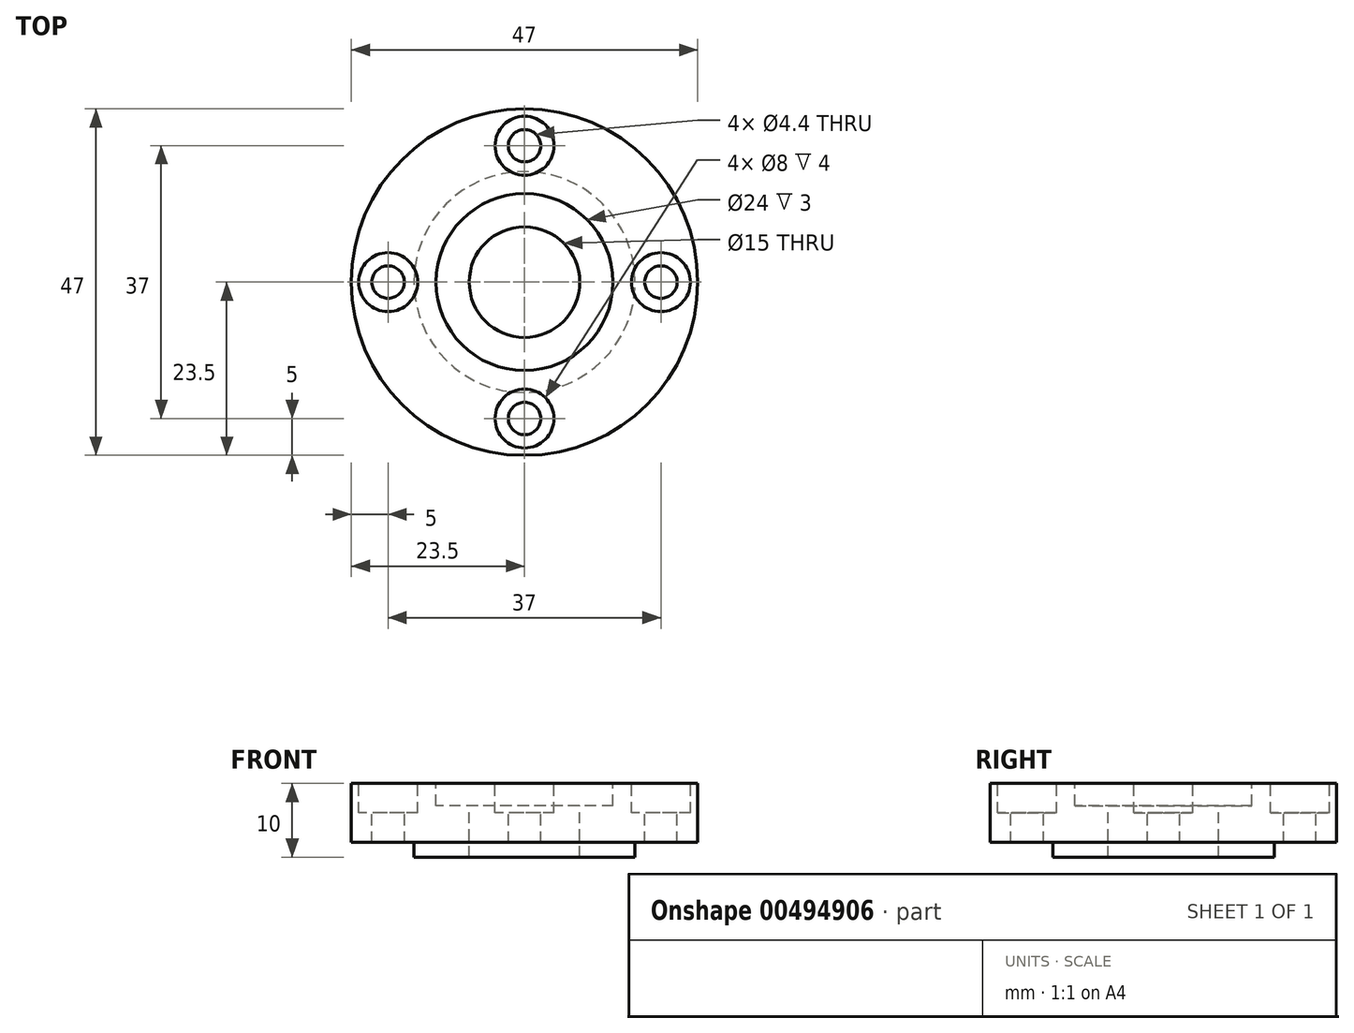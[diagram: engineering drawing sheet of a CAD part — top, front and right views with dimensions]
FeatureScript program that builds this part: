
annotation { "Feature Type Name" : "Feature", "Feature Type Description" : "" }
export const myFeature = defineFeature(function(context is Context, id is Id, definition is map)
    precondition{}
    {
        {
            var Q0;
            Q0=qCreatedBy(makeId("Top.planeOp"),FACE);
            var sketch = newSketch(context, id + "F0", { "sketchPlane" : qUnion([Q0])});
            skCircle(sketch, "E0", {"center": v(0, 0) * mm, "radius": 15 * mm});
            skSolve(sketch);
        }
        {
            var Q0;
            Q0=qSketchRegion(id+"F0",true);
            extrude(context, id + "F1", {"entities" : qUnion([Q0]), "oppositeDirection" : true, "depth" : 2 * mm});
        }
        {
            var Q0;
            Q0=qCreatedBy(makeId("Top.planeOp"),FACE);
            var sketch = newSketch(context, id + "F2", { "sketchPlane" : qUnion([Q0])});
            skCircle(sketch, "E1", {"center": v(0, 0) * mm, "radius": 23.5 * mm});
            skSolve(sketch);
        }
        {
            var Q0;
            Q0=qSketchRegion(id+"F2",true);
            extrude(context, id + "F3", {"entities" : qUnion([Q0]), "operationType" : NewBodyOperationType.ADD, "depth" : 8 * mm});
        }
        {
            var Q0;
            Q0=makeQuery(id+"F3.opExtrude","CAP_FACE",FACE,{"disambiguationData":[OSD([sQuery(id+"F2.wireOp",EDGE,"E1")])],"isStart":false});
            var sketch = newSketch(context, id + "F4", { "sketchPlane" : qUnion([Q0])});
            skCircle(sketch, "E2", {"center": v(0, 0) * mm, "radius": 12 * mm});
            skSolve(sketch);
        }
        {
            var Q0;
            Q0=qSketchRegion(id+"F4",true);
            extrude(context, id + "F5", {"entities" : qUnion([Q0]), "operationType" : NewBodyOperationType.REMOVE, "oppositeDirection" : true, "depth" : 3 * mm});
        }
        {
            var Q0;
            Q0=makeQuery(id+"F5.boolean.opBoolean","COPY",FACE,{"derivedFrom":makeQuery(id+"F5.opExtrude","CAP_FACE",FACE,{"disambiguationData":[OSD([sQuery(id+"F4.wireOp",EDGE,"E2")])],"isStart":false})});
            var sketch = newSketch(context, id + "F6", { "sketchPlane" : qUnion([Q0])});
            skCircle(sketch, "E3", {"center": v(0, 0) * mm, "radius": 7.5 * mm});
            skSolve(sketch);
        }
        {
            var Q0;
            Q0=qSketchRegion(id+"F6",true);
            extrude(context, id + "F7", {"entities" : qUnion([Q0]), "operationType" : NewBodyOperationType.REMOVE, "endBound" : BoundingType.THROUGH_ALL, "oppositeDirection" : true, "depth" : 25 * mm});
        }
        {
            var Q0;
            Q0=makeQuery(id+"F3.opExtrude","CAP_FACE",FACE,{"disambiguationData":[OSD([sQuery(id+"F2.wireOp",EDGE,"E1")])],"isStart":false});
            var sketch = newSketch(context, id + "F8", { "sketchPlane" : qUnion([Q0])});
            skPoint(sketch, "E4", {"position": v(0, 18.5) * mm});
            skPoint(sketch, "E5", {"position": v(18.5, 0) * mm});
            skPoint(sketch, "E6", {"position": v(0, -18.5) * mm});
            skPoint(sketch, "E7", {"position": v(-18.5, 0) * mm});
            skSolve(sketch);
        }
        {
            var Q0;
            Q0=sQuery(id+"F8.wireOp",VERTEX,"E4");
            var Q1;
            Q1=sQuery(id+"F8.wireOp",VERTEX,"E7");
            var Q2;
            Q2=sQuery(id+"F8.wireOp",VERTEX,"E6");
            var Q3;
            Q3=sQuery(id+"F8.wireOp",VERTEX,"E5");
            var Q4;
            Q4=makeQuery(id+"F1.opExtrude","SWEPT_BODY",BODY,{"disambiguationData":[OSD([sQuery(id+"F0.wireOp",EDGE,"E0")])]});
            hole(context, id + "F9", {"style" : HoleStyle.C_BORE, "endStyle" : HoleEndStyle.THROUGH, "holeDiameter" : 4.4 * mm, "cBoreDiameter" : 8 * mm, "cBoreDepth" : 4 * mm, "isTappedThrough" : true, "tappedDepth" : 12.25 * mm, "tapClearance" : 3, "locations" : qUnion([Q0, Q1, Q2, Q3]), "scope" : qUnion([Q4])});
        }
    });
